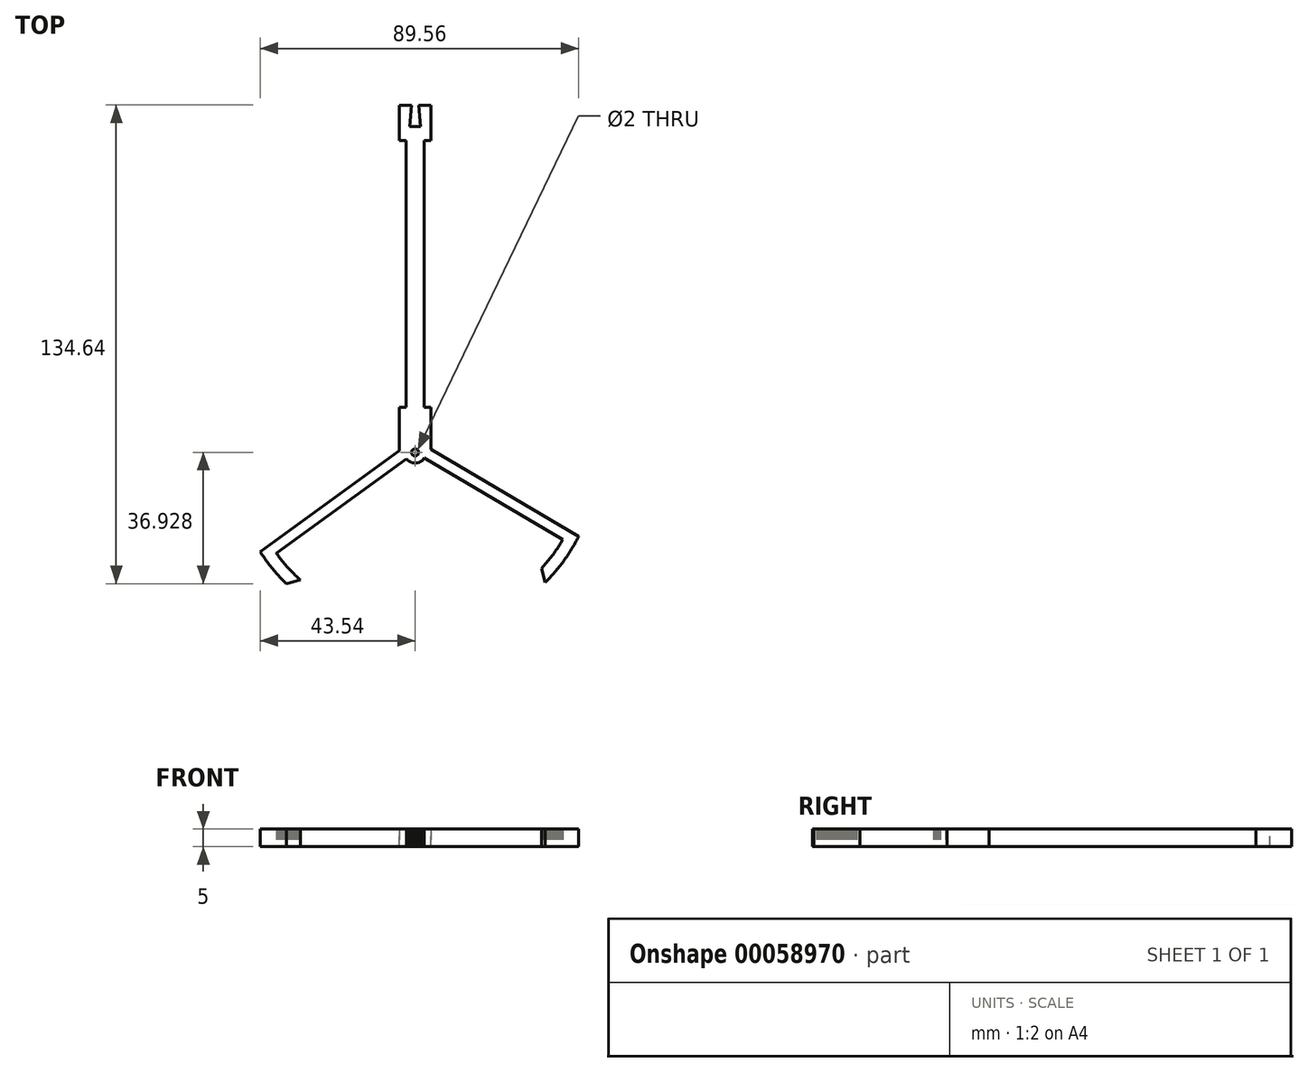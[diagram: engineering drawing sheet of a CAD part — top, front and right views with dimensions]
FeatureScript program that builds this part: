
annotation { "Feature Type Name" : "Feature", "Feature Type Description" : "" }
export const myFeature = defineFeature(function(context is Context, id is Id, definition is map)
    precondition{}
    {
        {
            var Q0;
            Q0=qCreatedBy(makeId("Top.planeOp"),FACE);
            var sketch = newSketch(context, id + "F0", { "sketchPlane" : qUnion([Q0])});
            skLineSegment(sketch, "E0.top", {"start": v(3.2, 29.68) * mm, "end": v(-5.68, 29.68) * mm});
            skLineSegment(sketch, "E0.left", {"start": v(3.2, 16.97) * mm, "end": v(3.2, 29.68) * mm});
            skLineSegment(sketch, "E0.right", {"start": v(-5.68, 16.97) * mm, "end": v(-5.68, 29.68) * mm});
            skLineSegment(sketch, "E1", {"start": v(-5.68, 16.97) * mm, "end": v(3.2, 16.97) * mm});
            skLineSegment(sketch, "E2", {"start": v(-33.5, -18.91) * mm, "end": v(-33.88, -18.58) * mm});
            skLineSegment(sketch, "E3", {"start": v(-33.88, -18.58) * mm, "end": v(-34.24, -18.24) * mm});
            skLineSegment(sketch, "E4", {"start": v(-34.24, -18.24) * mm, "end": v(-34.6, -17.9) * mm});
            skLineSegment(sketch, "E5", {"start": v(-34.6, -17.9) * mm, "end": v(-34.97, -17.55) * mm});
            skLineSegment(sketch, "E6", {"start": v(-34.97, -17.55) * mm, "end": v(-35.32, -17.2) * mm});
            skLineSegment(sketch, "E7", {"start": v(-35.32, -17.2) * mm, "end": v(-35.67, -16.84) * mm});
            skLineSegment(sketch, "E8", {"start": v(-35.67, -16.84) * mm, "end": v(-36.02, -16.48) * mm});
            skLineSegment(sketch, "E9", {"start": v(-36.02, -16.48) * mm, "end": v(-36.37, -16.12) * mm});
            skLineSegment(sketch, "E10", {"start": v(-36.37, -16.12) * mm, "end": v(-36.7, -15.75) * mm});
            skLineSegment(sketch, "E11", {"start": v(-36.7, -15.75) * mm, "end": v(-37.05, -15.38) * mm});
            skLineSegment(sketch, "E12", {"start": v(-37.05, -15.38) * mm, "end": v(-37.38, -15.01) * mm});
            skLineSegment(sketch, "E13", {"start": v(-37.38, -15.01) * mm, "end": v(-37.7, -14.64) * mm});
            skLineSegment(sketch, "E14", {"start": v(-37.7, -14.64) * mm, "end": v(-38.03, -14.26) * mm});
            skLineSegment(sketch, "E15", {"start": v(-38.03, -14.26) * mm, "end": v(-38.36, -13.87) * mm});
            skLineSegment(sketch, "E16", {"start": v(-38.36, -13.87) * mm, "end": v(-38.67, -13.49) * mm});
            skLineSegment(sketch, "E17", {"start": v(-38.67, -13.49) * mm, "end": v(-38.99, -13.1) * mm});
            skLineSegment(sketch, "E18", {"start": v(-38.99, -13.1) * mm, "end": v(-39.3, -12.7) * mm});
            skLineSegment(sketch, "E19", {"start": v(-39.3, -12.7) * mm, "end": v(-39.6, -12.3) * mm});
            skLineSegment(sketch, "E20", {"start": v(-39.6, -12.3) * mm, "end": v(-39.9, -11.9) * mm});
            skLineSegment(sketch, "E21", {"start": v(-39.9, -11.9) * mm, "end": v(-40.2, -11.5) * mm});
            skLineSegment(sketch, "E22", {"start": v(-40.2, -11.5) * mm, "end": v(-40.26, -11.42) * mm});
            skLineSegment(sketch, "E23", {"start": v(-40.26, -11.42) * mm, "end": v(-3.67, 15.2) * mm});
            skLineSegment(sketch, "E24", {"start": v(-3.67, 15.2) * mm, "end": v(-3.34, 14.82) * mm});
            skLineSegment(sketch, "E25", {"start": v(-3.34, 14.82) * mm, "end": v(-2.95, 14.5) * mm});
            skLineSegment(sketch, "E26", {"start": v(-2.95, 14.5) * mm, "end": v(-2.52, 14.25) * mm});
            skLineSegment(sketch, "E27", {"start": v(-2.52, 14.25) * mm, "end": v(-2.06, 14.08) * mm});
            skLineSegment(sketch, "E28", {"start": v(-2.06, 14.08) * mm, "end": v(-1.56, 13.98) * mm});
            skLineSegment(sketch, "E29", {"start": v(-1.56, 13.98) * mm, "end": v(-1.07, 13.97) * mm});
            skLineSegment(sketch, "E30", {"start": v(-1.07, 13.97) * mm, "end": v(-0.57, 14.04) * mm});
            skLineSegment(sketch, "E31", {"start": v(-0.57, 14.04) * mm, "end": v(-0.1, 14.2) * mm});
            skLineSegment(sketch, "E32", {"start": v(-0.1, 14.2) * mm, "end": v(0.35, 14.42) * mm});
            skLineSegment(sketch, "E33", {"start": v(0.35, 14.42) * mm, "end": v(0.75, 14.72) * mm});
            skLineSegment(sketch, "E34", {"start": v(0.75, 14.72) * mm, "end": v(1.1, 15.08) * mm});
            skLineSegment(sketch, "E35", {"start": v(1.1, 15.08) * mm, "end": v(1.34, 15.44) * mm});
            skLineSegment(sketch, "E36", {"start": v(1.34, 15.44) * mm, "end": v(40.32, -7.55) * mm});
            skLineSegment(sketch, "E37", {"start": v(40.32, -7.55) * mm, "end": v(40.07, -7.98) * mm});
            skLineSegment(sketch, "E38", {"start": v(40.07, -7.98) * mm, "end": v(39.8, -8.4) * mm});
            skLineSegment(sketch, "E39", {"start": v(39.8, -8.4) * mm, "end": v(39.54, -8.83) * mm});
            skLineSegment(sketch, "E40", {"start": v(39.54, -8.83) * mm, "end": v(39.27, -9.25) * mm});
            skLineSegment(sketch, "E41", {"start": v(39.27, -9.25) * mm, "end": v(39, -9.67) * mm});
            skLineSegment(sketch, "E42", {"start": v(39, -9.67) * mm, "end": v(38.72, -10.09) * mm});
            skLineSegment(sketch, "E43", {"start": v(38.72, -10.09) * mm, "end": v(38.44, -10.5) * mm});
            skLineSegment(sketch, "E44", {"start": v(38.44, -10.5) * mm, "end": v(38.15, -10.9) * mm});
            skLineSegment(sketch, "E45", {"start": v(38.15, -10.9) * mm, "end": v(37.86, -11.31) * mm});
            skLineSegment(sketch, "E46", {"start": v(37.86, -11.31) * mm, "end": v(37.57, -11.72) * mm});
            skLineSegment(sketch, "E47", {"start": v(37.57, -11.72) * mm, "end": v(37.27, -12.12) * mm});
            skLineSegment(sketch, "E48", {"start": v(37.27, -12.12) * mm, "end": v(36.96, -12.52) * mm});
            skLineSegment(sketch, "E49", {"start": v(36.96, -12.52) * mm, "end": v(36.65, -12.91) * mm});
            skLineSegment(sketch, "E50", {"start": v(36.65, -12.91) * mm, "end": v(36.34, -13.3) * mm});
            skLineSegment(sketch, "E51", {"start": v(36.34, -13.3) * mm, "end": v(36.03, -13.69) * mm});
            skLineSegment(sketch, "E52", {"start": v(36.03, -13.69) * mm, "end": v(35.7, -14.07) * mm});
            skLineSegment(sketch, "E53", {"start": v(35.7, -14.07) * mm, "end": v(35.38, -14.45) * mm});
            skLineSegment(sketch, "E54", {"start": v(35.38, -14.45) * mm, "end": v(35.06, -14.83) * mm});
            skLineSegment(sketch, "E55", {"start": v(35.06, -14.83) * mm, "end": v(34.73, -15.2) * mm});
            skLineSegment(sketch, "E56", {"start": v(34.73, -15.2) * mm, "end": v(34.4, -15.58) * mm});
            skLineSegment(sketch, "E57", {"start": v(34.4, -15.58) * mm, "end": v(34.32, -15.66) * mm});
            skLineSegment(sketch, "E58", {"start": v(34.32, -15.66) * mm, "end": v(35.33, -19.65) * mm});
            skLineSegment(sketch, "E59", {"start": v(35.33, -19.65) * mm, "end": v(35.68, -19.3) * mm});
            skLineSegment(sketch, "E60", {"start": v(35.68, -19.3) * mm, "end": v(36.03, -18.93) * mm});
            skLineSegment(sketch, "E61", {"start": v(36.03, -18.93) * mm, "end": v(36.37, -18.57) * mm});
            skLineSegment(sketch, "E62", {"start": v(36.37, -18.57) * mm, "end": v(36.72, -18.2) * mm});
            skLineSegment(sketch, "E63", {"start": v(36.72, -18.2) * mm, "end": v(37.05, -17.84) * mm});
            skLineSegment(sketch, "E64", {"start": v(37.05, -17.84) * mm, "end": v(37.39, -17.47) * mm});
            skLineSegment(sketch, "E65", {"start": v(37.39, -17.47) * mm, "end": v(37.72, -17.1) * mm});
            skLineSegment(sketch, "E66", {"start": v(37.72, -17.1) * mm, "end": v(38.05, -16.71) * mm});
            skLineSegment(sketch, "E67", {"start": v(38.05, -16.71) * mm, "end": v(38.37, -16.33) * mm});
            skLineSegment(sketch, "E68", {"start": v(38.37, -16.33) * mm, "end": v(38.69, -15.95) * mm});
            skLineSegment(sketch, "E69", {"start": v(38.69, -15.95) * mm, "end": v(39, -15.56) * mm});
            skLineSegment(sketch, "E70", {"start": v(39, -15.56) * mm, "end": v(39.32, -15.17) * mm});
            skLineSegment(sketch, "E71", {"start": v(39.32, -15.17) * mm, "end": v(39.63, -14.78) * mm});
            skLineSegment(sketch, "E72", {"start": v(39.63, -14.78) * mm, "end": v(39.93, -14.38) * mm});
            skLineSegment(sketch, "E73", {"start": v(39.93, -14.38) * mm, "end": v(40.23, -13.98) * mm});
            skLineSegment(sketch, "E74", {"start": v(40.23, -13.98) * mm, "end": v(40.53, -13.58) * mm});
            skLineSegment(sketch, "E75", {"start": v(40.53, -13.58) * mm, "end": v(40.82, -13.17) * mm});
            skLineSegment(sketch, "E76", {"start": v(40.82, -13.17) * mm, "end": v(41.11, -12.77) * mm});
            skLineSegment(sketch, "E77", {"start": v(41.11, -12.77) * mm, "end": v(41.4, -12.35) * mm});
            skLineSegment(sketch, "E78", {"start": v(41.4, -12.35) * mm, "end": v(41.68, -11.94) * mm});
            skLineSegment(sketch, "E79", {"start": v(41.68, -11.94) * mm, "end": v(41.96, -11.53) * mm});
            skLineSegment(sketch, "E80", {"start": v(41.96, -11.53) * mm, "end": v(42.23, -11.1) * mm});
            skLineSegment(sketch, "E81", {"start": v(42.23, -11.1) * mm, "end": v(42.5, -10.69) * mm});
            skLineSegment(sketch, "E82", {"start": v(42.5, -10.69) * mm, "end": v(42.76, -10.26) * mm});
            skLineSegment(sketch, "E83", {"start": v(42.76, -10.26) * mm, "end": v(43.02, -9.83) * mm});
            skLineSegment(sketch, "E84", {"start": v(43.02, -9.83) * mm, "end": v(43.28, -9.4) * mm});
            skLineSegment(sketch, "E85", {"start": v(43.28, -9.4) * mm, "end": v(43.53, -8.97) * mm});
            skLineSegment(sketch, "E86", {"start": v(43.53, -8.97) * mm, "end": v(43.78, -8.54) * mm});
            skLineSegment(sketch, "E87", {"start": v(43.78, -8.54) * mm, "end": v(44.03, -8.1) * mm});
            skLineSegment(sketch, "E88", {"start": v(44.03, -8.1) * mm, "end": v(44.27, -7.67) * mm});
            skLineSegment(sketch, "E89", {"start": v(44.27, -7.67) * mm, "end": v(44.5, -7.22) * mm});
            skLineSegment(sketch, "E90", {"start": v(44.5, -7.22) * mm, "end": v(44.73, -6.78) * mm});
            skLineSegment(sketch, "E91", {"start": v(44.73, -6.78) * mm, "end": v(44.78, -6.7) * mm});
            skLineSegment(sketch, "E92", {"start": v(44.78, -6.7) * mm, "end": v(0.28, 19.55) * mm});
            skLineSegment(sketch, "E93", {"start": v(0.28, 19.55) * mm, "end": v(-0.17, 19.77) * mm});
            skLineSegment(sketch, "E94", {"start": v(-0.17, 19.77) * mm, "end": v(-0.65, 19.9) * mm});
            skLineSegment(sketch, "E95", {"start": v(-0.65, 19.9) * mm, "end": v(-1.14, 19.96) * mm});
            skLineSegment(sketch, "E96", {"start": v(-1.14, 19.96) * mm, "end": v(-1.64, 19.94) * mm});
            skLineSegment(sketch, "E97", {"start": v(-1.64, 19.94) * mm, "end": v(-2.13, 19.83) * mm});
            skLineSegment(sketch, "E98", {"start": v(-2.13, 19.83) * mm, "end": v(-2.6, 19.64) * mm});
            skLineSegment(sketch, "E99", {"start": v(-2.6, 19.64) * mm, "end": v(-3, 19.4) * mm});
            skLineSegment(sketch, "E100", {"start": v(-3, 19.4) * mm, "end": v(-44.78, -11) * mm});
            skLineSegment(sketch, "E101", {"start": v(-44.78, -11) * mm, "end": v(-44.5, -11.42) * mm});
            skLineSegment(sketch, "E102", {"start": v(-44.5, -11.42) * mm, "end": v(-44.23, -11.83) * mm});
            skLineSegment(sketch, "E103", {"start": v(-44.23, -11.83) * mm, "end": v(-43.95, -12.25) * mm});
            skLineSegment(sketch, "E104", {"start": v(-43.95, -12.25) * mm, "end": v(-43.67, -12.66) * mm});
            skLineSegment(sketch, "E105", {"start": v(-43.67, -12.66) * mm, "end": v(-43.38, -13.07) * mm});
            skLineSegment(sketch, "E106", {"start": v(-43.38, -13.07) * mm, "end": v(-43.09, -13.47) * mm});
            skLineSegment(sketch, "E107", {"start": v(-43.09, -13.47) * mm, "end": v(-42.79, -13.88) * mm});
            skLineSegment(sketch, "E108", {"start": v(-42.79, -13.88) * mm, "end": v(-42.49, -14.28) * mm});
            skLineSegment(sketch, "E109", {"start": v(-42.49, -14.28) * mm, "end": v(-42.19, -14.67) * mm});
            skLineSegment(sketch, "E110", {"start": v(-42.19, -14.67) * mm, "end": v(-41.88, -15.07) * mm});
            skLineSegment(sketch, "E111", {"start": v(-41.88, -15.07) * mm, "end": v(-41.57, -15.46) * mm});
            skLineSegment(sketch, "E112", {"start": v(-41.57, -15.46) * mm, "end": v(-41.25, -15.85) * mm});
            skLineSegment(sketch, "E113", {"start": v(-41.25, -15.85) * mm, "end": v(-40.93, -16.23) * mm});
            skLineSegment(sketch, "E114", {"start": v(-40.93, -16.23) * mm, "end": v(-40.6, -16.61) * mm});
            skLineSegment(sketch, "E115", {"start": v(-40.6, -16.61) * mm, "end": v(-40.28, -17) * mm});
            skLineSegment(sketch, "E116", {"start": v(-40.28, -17) * mm, "end": v(-39.95, -17.37) * mm});
            skLineSegment(sketch, "E117", {"start": v(-39.95, -17.37) * mm, "end": v(-39.62, -17.74) * mm});
            skLineSegment(sketch, "E118", {"start": v(-39.62, -17.74) * mm, "end": v(-39.28, -18.11) * mm});
            skLineSegment(sketch, "E119", {"start": v(-39.28, -18.11) * mm, "end": v(-38.94, -18.48) * mm});
            skLineSegment(sketch, "E120", {"start": v(-38.94, -18.48) * mm, "end": v(-38.6, -18.84) * mm});
            skLineSegment(sketch, "E121", {"start": v(-38.6, -18.84) * mm, "end": v(-38.25, -19.2) * mm});
            skLineSegment(sketch, "E122", {"start": v(-38.25, -19.2) * mm, "end": v(-37.9, -19.55) * mm});
            skLineSegment(sketch, "E123", {"start": v(-37.9, -19.55) * mm, "end": v(-37.54, -19.9) * mm});
            skLineSegment(sketch, "E124", {"start": v(-37.54, -19.9) * mm, "end": v(-37.49, -19.96) * mm});
            skLineSegment(sketch, "E125", {"start": v(-37.49, -19.96) * mm, "end": v(-33.5, -18.91) * mm});
            skLineSegment(sketch, "E126", {"start": v(-2.24, 16.97) * mm, "end": v(-0.24, 16.97) * mm, "construction": true});
            skPoint(sketch, "E127", {"position": v(-1.24, 16.97) * mm});
            skCircle(sketch, "E128", {"center": v(-1.24, 16.97) * mm, "radius": 1 * mm});
            skSolve(sketch);
        }
        {
            var Q0;
            Q0=qSketchRegion(id+"F0",true);
            extrude(context, id + "F1", {"entities" : qUnion([Q0]), "depth" : 5 * mm});
        }
        {
            var Q0;
            Q0=makeQuery(id+"F1.opExtrude","SWEPT_FACE",FACE,{"disambiguationData":[OSD([sQuery(id+"F0.wireOp",EDGE,"E0.top")])]});
            var sketch = newSketch(context, id + "F2", { "sketchPlane" : qUnion([Q0])});
            skLineSegment(sketch, "E129.bottom", {"start": v(-3.2, 5) * mm, "end": v(5.68, 5) * mm, "construction": true});
            skLineSegment(sketch, "E129.top", {"start": v(-3.2, 0) * mm, "end": v(5.68, 0) * mm, "construction": true});
            skLineSegment(sketch, "E129.left", {"start": v(-3.2, 5) * mm, "end": v(-3.2, 0) * mm, "construction": true});
            skLineSegment(sketch, "E129.right", {"start": v(5.68, 5) * mm, "end": v(5.68, 0) * mm, "construction": true});
            skLineSegment(sketch, "E130", {"start": v(1.24, 5) * mm, "end": v(1.24, 0) * mm, "construction": true});
            skPoint(sketch, "E131", {"position": v(1.24, 2.5) * mm});
            skLineSegment(sketch, "E132.bottom", {"start": v(-1.26, 5) * mm, "end": v(3.74, 5) * mm});
            skLineSegment(sketch, "E132.top", {"start": v(-1.26, 0) * mm, "end": v(3.74, 0) * mm});
            skLineSegment(sketch, "E132.left", {"start": v(-1.26, 5) * mm, "end": v(-1.26, 0) * mm});
            skLineSegment(sketch, "E132.right", {"start": v(3.74, 5) * mm, "end": v(3.74, 0) * mm});
            skPoint(sketch, "E133", {"position": v(1.24, 5) * mm});
            skSolve(sketch);
        }
        {
            var Q0;
            Q0=makeQuery(id+"F2.imprint","IMPRINT",FACE,{"disambiguationData":[TD([[makeQuery(id+"F2.imprint","IMPRINT",EDGE,{"derivedFrom":sQuery(id+"F2.wireOp",EDGE,"E132.bottom")}),-1.0]])]});
            extrude(context, id + "F3", {"entities" : qUnion([Q0]), "operationType" : NewBodyOperationType.ADD, "depth" : 85 * mm});
        }
        {
            var Q0;
            Q0=makeQuery(id+"F3.boolean.opBoolean","MERGE",FACE,{"derivedFrom":[makeQuery(id+"F1.opExtrude","CAP_FACE",FACE,{"disambiguationData":[OSD([sQuery(id+"F0.wireOp",EDGE,"d9f391bc-674f-497b-be90-560cbfe84b75"),sQuery(id+"F0.wireOp",EDGE,"66b45562-6a73-478d-960d-9298d4f6f7f0"),sQuery(id+"F0.wireOp",EDGE,"14187485-9066-4405-92d3-fc27601e42af"),sQuery(id+"F0.wireOp",EDGE,"531d857a-c366-4fd6-946f-2a201ec59503"),sQuery(id+"F0.wireOp",EDGE,"82b77f9d-e961-41ac-b487-f27284012814"),sQuery(id+"F0.wireOp",EDGE,"7834417a-5e7c-45c5-8e6f-19fbc39ef538"),sQuery(id+"F0.wireOp",EDGE,"300af05a-1d2d-4a39-b159-b80513d7f740"),sQuery(id+"F0.wireOp",EDGE,"1d5f7e8b-d76f-446f-8b3e-2a2f550bd8e3"),sQuery(id+"F0.wireOp",EDGE,"35e8518a-73fa-4b07-8810-64eb534e7b1e"),sQuery(id+"F0.wireOp",EDGE,"18614789-dbbf-47a7-80e0-906205be91d2"),sQuery(id+"F0.wireOp",EDGE,"b77e8b2d-b58d-4b65-9e12-d4334338aa4c"),sQuery(id+"F0.wireOp",EDGE,"9d96ad04-3b06-4638-bbb7-3f0403701198"),sQuery(id+"F0.wireOp",EDGE,"e2f941ec-7ca7-4e10-9b82-3674a8dee568"),sQuery(id+"F0.wireOp",EDGE,"623cfd6c-6096-4034-a234-787e3acb7919"),sQuery(id+"F0.wireOp",EDGE,"effc0b7c-bb45-4b4c-82cf-5a194e7747a9"),sQuery(id+"F0.wireOp",EDGE,"20afc2aa-4987-4b9c-837f-1a90a823d70c"),sQuery(id+"F0.wireOp",EDGE,"93c108a5-420a-46d6-a4f1-9fc166012f6e"),sQuery(id+"F0.wireOp",EDGE,"24f54e41-abe2-49ed-aca4-37dbfc811c90"),sQuery(id+"F0.wireOp",EDGE,"9775e243-409f-4585-bc05-4883512e3564"),sQuery(id+"F0.wireOp",EDGE,"a5e87a16-9f3d-4e96-afb7-1f3010025381"),sQuery(id+"F0.wireOp",EDGE,"57da4376-ad28-41da-a036-1c08f5a0e9fe"),sQuery(id+"F0.wireOp",EDGE,"42ac5c60-1a59-4eb0-a50e-105db2941719"),sQuery(id+"F0.wireOp",EDGE,"7f869c91-c514-4a78-955d-8fa2f71ec013"),sQuery(id+"F0.wireOp",EDGE,"92df5dc1-1633-40e4-82dc-26b14e9fc4fe"),sQuery(id+"F0.wireOp",EDGE,"9fb6344f-8160-4d43-a8ca-7dc5bcb63cf4"),sQuery(id+"F0.wireOp",EDGE,"403433ed-74ab-49ef-b5f3-8321a2a46bc0"),sQuery(id+"F0.wireOp",EDGE,"38791a52-10f3-4032-89cb-9997d4a285ff"),sQuery(id+"F0.wireOp",EDGE,"17827bc5-de02-4b8f-ae35-e25ffe9a3a56"),sQuery(id+"F0.wireOp",EDGE,"ebb8a741-28c9-44e3-8d01-7b9906950363"),sQuery(id+"F0.wireOp",EDGE,"24247562-824f-4080-b562-a07a46203f45"),sQuery(id+"F0.wireOp",EDGE,"61158206-3902-44f4-b84a-59a3b62cea53"),sQuery(id+"F0.wireOp",EDGE,"222b9068-06c2-468c-a816-7dcc0e9861e7"),sQuery(id+"F0.wireOp",EDGE,"1443c47e-cb78-4972-aa1d-b2a5593cacaa"),sQuery(id+"F0.wireOp",EDGE,"4ee5fa2a-e4b7-4507-9879-d4257c452374"),sQuery(id+"F0.wireOp",EDGE,"ac129c3d-c943-4e23-b628-d4f0035e9390"),sQuery(id+"F0.wireOp",EDGE,"a4b60933-6dc5-485c-afad-bad217473213"),sQuery(id+"F0.wireOp",EDGE,"c784899e-bd4b-4296-9021-59274ccaadd9"),sQuery(id+"F0.wireOp",EDGE,"748fc19f-7cd7-4142-921c-8b19d610d3d1"),sQuery(id+"F0.wireOp",EDGE,"ebea3f07-4c38-41c4-ac2c-bac9cb8d1528"),sQuery(id+"F0.wireOp",EDGE,"c6bc3915-ea64-408b-b0c0-442b260292ac"),sQuery(id+"F0.wireOp",EDGE,"15593884-b140-4daf-bfd8-0ecfa5efcbbd"),sQuery(id+"F0.wireOp",EDGE,"a7df4056-7cd6-44bf-9033-605bc9c32d03"),sQuery(id+"F0.wireOp",EDGE,"39d318a8-1c2b-49b4-b444-523ba4d5fcf2"),sQuery(id+"F0.wireOp",EDGE,"11df0492-6635-41a9-8511-0c760388fa34"),sQuery(id+"F0.wireOp",EDGE,"a12d8f92-446a-4b34-a2f5-26c26993d257"),sQuery(id+"F0.wireOp",EDGE,"78a7d225-68f4-4e83-b71e-32c50f125e93"),sQuery(id+"F0.wireOp",EDGE,"1862a963-57d5-471d-8109-9f73d1aa8848"),sQuery(id+"F0.wireOp",EDGE,"54f45445-f8d1-4aff-bece-9da66ad386cd"),sQuery(id+"F0.wireOp",EDGE,"5ba05bdf-983b-4f68-941c-4bf50adfb3c5"),sQuery(id+"F0.wireOp",EDGE,"973eaeb2-d25f-40eb-b74f-e363d637089d"),sQuery(id+"F0.wireOp",EDGE,"9fe65cb9-7a78-4622-86d1-7f23de040810"),sQuery(id+"F0.wireOp",EDGE,"3fe47919-788c-4396-b5fd-8990ec275c22"),sQuery(id+"F0.wireOp",EDGE,"55bf8aa7-cfd1-4645-9e83-de087904feb2"),sQuery(id+"F0.wireOp",EDGE,"c2af9e0f-cc3a-474c-a54e-54ce149af3bb"),sQuery(id+"F0.wireOp",EDGE,"ff518af7-eed7-424f-ad46-c5242196626b"),sQuery(id+"F0.wireOp",EDGE,"cc0332f5-aef5-4de5-a14e-8dcbe21eca6c"),sQuery(id+"F0.wireOp",EDGE,"c5d08f8f-8ed2-45eb-9a75-cb5f251a4d6d"),sQuery(id+"F0.wireOp",EDGE,"5995e242-d37b-4450-9f63-962c7eb38085"),sQuery(id+"F0.wireOp",EDGE,"25f3b115-5ae4-4790-92e5-62a7bc3f5c29"),sQuery(id+"F0.wireOp",EDGE,"2d611a70-a2f5-475a-a6a8-adddd76473ce"),sQuery(id+"F0.wireOp",EDGE,"273bf26d-3f66-4ef4-bf64-d22a533f903a"),sQuery(id+"F0.wireOp",EDGE,"de5f23e0-e1a0-4e15-900e-688ab9168dcd"),sQuery(id+"F0.wireOp",EDGE,"4de6b542-ff3a-44f7-b58e-1e4f3b2cccf4"),sQuery(id+"F0.wireOp",EDGE,"be1b36f0-e020-4af0-baec-c4481b6b9122"),sQuery(id+"F0.wireOp",EDGE,"d7c1d08a-2f0c-4649-94c4-8f89162c768a"),sQuery(id+"F0.wireOp",EDGE,"bd09b6b8-9bc9-4c5b-ab2b-4ede4d9b9cae"),sQuery(id+"F0.wireOp",EDGE,"05b5a1f0-0223-4439-ac6f-cac7d6a05357"),sQuery(id+"F0.wireOp",EDGE,"318e3676-c449-41e0-b4da-e74d07fc2b12"),sQuery(id+"F0.wireOp",EDGE,"31725f89-0695-4483-9200-5756053d80e4"),sQuery(id+"F0.wireOp",EDGE,"e3cb0712-5583-40de-9f57-2bae5fcde790"),sQuery(id+"F0.wireOp",EDGE,"c6456fea-21fc-4931-a427-a856d1f6ee5c"),sQuery(id+"F0.wireOp",EDGE,"e7d8b0b0-a421-4050-b770-ef5136dc3e4d"),sQuery(id+"F0.wireOp",EDGE,"0788d0b0-f754-45d8-aefc-a91755a03ac1"),sQuery(id+"F0.wireOp",EDGE,"fc27efed-591c-43cc-b4b2-6872e1742544"),sQuery(id+"F0.wireOp",EDGE,"82c2f9b8-58bc-4a33-9bd5-fec435af3e72"),sQuery(id+"F0.wireOp",EDGE,"2e300663-fb6b-4f29-9ebf-a9fab34af9c4"),sQuery(id+"F0.wireOp",EDGE,"3d2dfd07-a0b9-43b8-893f-685d0a355372"),sQuery(id+"F0.wireOp",EDGE,"e776ef69-6530-4f3d-8924-f9840dcd9e4d"),sQuery(id+"F0.wireOp",EDGE,"6dcbcc22-e493-4400-9b8a-7eed73031bc4"),sQuery(id+"F0.wireOp",EDGE,"7cdd9895-84d3-47ea-86bd-688608d79eca"),sQuery(id+"F0.wireOp",EDGE,"3a7bfdfd-3144-4dae-8888-a8bcf2221552"),sQuery(id+"F0.wireOp",EDGE,"2953d7e0-23a1-472e-bf8c-49982d9a56d6"),sQuery(id+"F0.wireOp",EDGE,"846718aa-0a8a-476e-8a52-f2d355658347"),sQuery(id+"F0.wireOp",EDGE,"13e02fad-2dbd-4394-a12b-883b621fb0cf"),sQuery(id+"F0.wireOp",EDGE,"9bfc4f6e-5194-4c80-9375-02c13d7037c7"),sQuery(id+"F0.wireOp",EDGE,"4cc90906-b22a-4bfe-9933-4a2b42c67043"),sQuery(id+"F0.wireOp",EDGE,"c3968d64-93bc-4dc6-b8a7-840e206f0e92"),sQuery(id+"F0.wireOp",EDGE,"cff9c3c0-4237-426c-aea8-7115d6da3525"),sQuery(id+"F0.wireOp",EDGE,"76e5b534-b14d-4a45-9111-d87c94f3d3da"),sQuery(id+"F0.wireOp",EDGE,"96eb4b59-6d18-41e9-8181-93777d457c04"),sQuery(id+"F0.wireOp",EDGE,"4b80822d-625d-4929-946d-bb2fee906de1"),sQuery(id+"F0.wireOp",EDGE,"a1b1815c-0f60-4723-aacc-aafe0ccbf065"),sQuery(id+"F0.wireOp",EDGE,"63631a9c-c3d0-4e34-b42e-cf718a2aa654"),sQuery(id+"F0.wireOp",EDGE,"291662e0-8a9a-4794-9b05-15f69232fded"),sQuery(id+"F0.wireOp",EDGE,"c31bbd6a-e51d-4bda-bb55-a930242c1aae"),sQuery(id+"F0.wireOp",EDGE,"6cc65a5c-01cd-414d-b4bf-16365d086d8b"),sQuery(id+"F0.wireOp",EDGE,"0f6044bc-5aed-4332-8dd0-ed4f837cf9c8"),sQuery(id+"F0.wireOp",EDGE,"68f51909-fb33-4c21-8354-d3ee43222832"),sQuery(id+"F0.wireOp",EDGE,"0ba4c335-165f-4c3e-a523-b257962ab2b9"),sQuery(id+"F0.wireOp",EDGE,"a8ab603d-6f8c-4c2b-bc3e-a90f3d25e983"),sQuery(id+"F0.wireOp",EDGE,"3346a9eb-c449-4294-82ff-d0765618b8c3"),sQuery(id+"F0.wireOp",EDGE,"efd91459-38fa-452e-891e-edab332f6489"),sQuery(id+"F0.wireOp",EDGE,"85b94afd-6a00-47ab-a374-eb0a6b957af6"),sQuery(id+"F0.wireOp",EDGE,"71bbe033-8d0c-4649-8752-095e423e4446"),sQuery(id+"F0.wireOp",EDGE,"313f4505-8deb-44f7-a07b-deab9fdd4fca"),sQuery(id+"F0.wireOp",EDGE,"58514e34-5bb3-46cf-af5d-05d66b0c10f9"),sQuery(id+"F0.wireOp",EDGE,"9c61e8f2-2ab1-4688-a9d6-5c20a88d6f6a"),sQuery(id+"F0.wireOp",EDGE,"f84fcc24-327f-4d24-8afc-1352f07d6813"),sQuery(id+"F0.wireOp",EDGE,"2217ef4b-fa2d-4c42-8d86-ed7db710f5bd"),sQuery(id+"F0.wireOp",EDGE,"d87f30a8-b645-4562-81e4-3c3cf9cd6438"),sQuery(id+"F0.wireOp",EDGE,"6b1cc9ff-038e-4fc2-952b-8fefe25711b2"),sQuery(id+"F0.wireOp",EDGE,"9b0d0940-50e4-4c60-959e-8cb1c47cda3d"),sQuery(id+"F0.wireOp",EDGE,"fd67a80c-15d7-4a10-bc2d-74f667f92aae"),sQuery(id+"F0.wireOp",EDGE,"ce9cbc48-37c6-4742-bee7-228e45a917e3"),sQuery(id+"F0.wireOp",EDGE,"668236f6-3d49-4ccf-890f-7b693b95a113"),sQuery(id+"F0.wireOp",EDGE,"f978c870-af19-49dc-a3f6-58e714ba6b8d"),sQuery(id+"F0.wireOp",EDGE,"3c9fd5d7-5c91-4e2a-8e90-77909dfb583b"),sQuery(id+"F0.wireOp",EDGE,"3f653433-d41a-442d-9af1-f4ba11755801"),sQuery(id+"F0.wireOp",EDGE,"3e1bc7f2-4028-408e-8046-60d3c4eab3db"),sQuery(id+"F0.wireOp",EDGE,"6e5cb531-4b2f-424d-b6a2-fd274bbfcedc"),sQuery(id+"F0.wireOp",EDGE,"47450d10-22bf-4260-9408-7e53fd283f2d"),sQuery(id+"F0.wireOp",EDGE,"6d45c327-3d4d-4948-b28d-f57c85b01b79"),sQuery(id+"F0.wireOp",EDGE,"09a427cb-33ca-4fdc-b261-2336e21235b2"),sQuery(id+"F0.wireOp",EDGE,"518944ec-1655-4f40-b183-544c6dabeccc"),sQuery(id+"F0.wireOp",EDGE,"9a21c479-1b04-474c-b49a-7bb92b3e97ee"),sQuery(id+"F0.wireOp",EDGE,"96faa4f8-2343-44d0-b0c9-daf9f0cf2026"),sQuery(id+"F0.wireOp",EDGE,"6fc17f55-5333-4b57-a339-275bf10e1425"),sQuery(id+"F0.wireOp",EDGE,"42fdd7f3-cbb8-400e-a0d9-d82489298c17"),sQuery(id+"F0.wireOp",EDGE,"ff3833a1-8283-4137-914b-97420855596c"),sQuery(id+"F0.wireOp",EDGE,"6d86c47c-1e01-4b32-ae2a-396aeb5aa8c3"),sQuery(id+"F0.wireOp",EDGE,"3656029b-9af7-4a6b-91c7-0cb8f82c84b0"),sQuery(id+"F0.wireOp",EDGE,"c5a5c181-3903-47b5-9841-0451d0b8c190"),sQuery(id+"F0.wireOp",EDGE,"6b476b77-b2de-421b-b26d-88dcbb17dccc"),sQuery(id+"F0.wireOp",EDGE,"3d318069-a1b2-4ca5-910a-b32c13e6ff0f"),sQuery(id+"F0.wireOp",EDGE,"9330180f-a560-47bb-918b-d92eebda0b31"),sQuery(id+"F0.wireOp",EDGE,"b318f770-8e99-4d49-b667-ae16576ab8c5"),sQuery(id+"F0.wireOp",EDGE,"e8c7022b-339d-4a50-8e2c-c0ad6522d806"),sQuery(id+"F0.wireOp",EDGE,"e86b4955-e698-4ab7-84b9-7f9632085e45"),sQuery(id+"F0.wireOp",EDGE,"0c38cf30-4431-4dda-a171-e1c8e016ea24"),sQuery(id+"F0.wireOp",EDGE,"f094b2ba-6a66-4d13-8490-6bb0ce785aa8"),sQuery(id+"F0.wireOp",EDGE,"41e1ebd6-8c90-401f-a72a-f212800231e3"),sQuery(id+"F0.wireOp",EDGE,"40e70cb6-71ec-4d67-b914-e8ee82708b93"),sQuery(id+"F0.wireOp",EDGE,"13f06e0a-f10b-47e7-959c-6b309f65aed5"),sQuery(id+"F0.wireOp",EDGE,"3fa473f8-a0ea-440b-8ccf-443d736f73d8"),sQuery(id+"F0.wireOp",EDGE,"3ff53a63-1f71-4b9e-b5b1-fe861864c7b9"),sQuery(id+"F0.wireOp",EDGE,"9fd11a8c-801f-433b-8a68-149d040764ea"),sQuery(id+"F0.wireOp",EDGE,"2b57bb01-2787-4d2a-a1f7-a8f2ac708940"),sQuery(id+"F0.wireOp",EDGE,"b3a649f2-00b2-4941-a5f4-54f2790e47c9"),sQuery(id+"F0.wireOp",EDGE,"689af078-1fc4-4801-82f7-c259a968d8e3"),sQuery(id+"F0.wireOp",EDGE,"4afb566c-1766-4da3-aeca-2e561b661cbf"),sQuery(id+"F0.wireOp",EDGE,"afbdcd0b-9ccb-41a6-b5df-fe1bcf30544d"),sQuery(id+"F0.wireOp",EDGE,"0a1a2607-09d2-45da-b494-66f0f4572d53"),sQuery(id+"F0.wireOp",EDGE,"df9dc95f-9734-4203-a4b0-b50527c86d60"),sQuery(id+"F0.wireOp",EDGE,"868db6a5-4ab0-468d-816c-25f0bc18b053"),sQuery(id+"F0.wireOp",EDGE,"aaa1c0b5-afc6-4e25-82a0-d6f0aaf8ec45"),sQuery(id+"F0.wireOp",EDGE,"450ffb83-aa88-433e-99e9-7fc4bc443133"),sQuery(id+"F0.wireOp",EDGE,"7c9dc92b-bdbd-4c2f-ba2f-b681be311a02"),sQuery(id+"F0.wireOp",EDGE,"d8d805bb-8432-4448-99fe-12ddf517f87f"),sQuery(id+"F0.wireOp",EDGE,"e1c897c1-2833-4eab-81cd-6ccc64de02e8"),sQuery(id+"F0.wireOp",EDGE,"12eef9dd-bb38-451e-8b46-68758d02cc0e"),sQuery(id+"F0.wireOp",EDGE,"f6b90299-a189-4960-beb2-75c4f087d852"),sQuery(id+"F0.wireOp",EDGE,"d44cce74-31fd-4baf-a4a6-ccbb4521b524"),sQuery(id+"F0.wireOp",EDGE,"26311da7-8aed-42c2-aa0d-06719439663e"),sQuery(id+"F0.wireOp",EDGE,"bfe2dd46-ca33-42a6-b3e5-4bcb679aff27"),sQuery(id+"F0.wireOp",EDGE,"f7121924-5964-4ee7-8e7a-9366b6055faf"),sQuery(id+"F0.wireOp",EDGE,"baddc95a-3768-4696-a9fc-c3c93e777550"),sQuery(id+"F0.wireOp",EDGE,"4cbcd0b8-8d3f-4500-b314-949e4192bba6"),sQuery(id+"F0.wireOp",EDGE,"573feae8-dbb2-4ee3-84b1-a2f0e784b4ce"),sQuery(id+"F0.wireOp",EDGE,"1491502b-4fac-4339-bddb-72d872b244a9"),sQuery(id+"F0.wireOp",EDGE,"ed8966f0-f9a2-415f-b3ef-00e8bec5a987"),sQuery(id+"F0.wireOp",EDGE,"42659012-de86-4715-a0b8-c198bc09b6c3"),sQuery(id+"F0.wireOp",EDGE,"eba869ca-ba70-4ef3-90af-459470689084"),sQuery(id+"F0.wireOp",EDGE,"9875f08d-c713-4704-93cd-788487ec0e6b"),sQuery(id+"F0.wireOp",EDGE,"88c7c1a6-46c1-45f7-a284-4e760e0ff227"),sQuery(id+"F0.wireOp",EDGE,"7296298e-4422-4531-89ec-245f94a1b7ce"),sQuery(id+"F0.wireOp",EDGE,"d982fd75-f615-4661-88e5-4d338e35f5d6"),sQuery(id+"F0.wireOp",EDGE,"855cb7c2-4006-4b69-ae1d-061ed893761e"),sQuery(id+"F0.wireOp",EDGE,"25f14cae-63dd-43dd-a2cf-069ce091aab3"),sQuery(id+"F0.wireOp",EDGE,"8dd2c990-ce8b-4ae6-88a5-6f7d81b76fb7"),sQuery(id+"F0.wireOp",EDGE,"50c487b6-7ae5-43ad-9b89-c44e1cfbe420"),sQuery(id+"F0.wireOp",EDGE,"28defd30-3f37-4457-b5ce-98c8ab6f0938"),sQuery(id+"F0.wireOp",EDGE,"25b26be1-608d-4fca-8147-ce63c78e7ef9"),sQuery(id+"F0.wireOp",EDGE,"55286520-3f9c-4cb0-8993-b41f90c1e7b2"),sQuery(id+"F0.wireOp",EDGE,"8b04d12e-496a-4f5a-9f87-f93561172584"),sQuery(id+"F0.wireOp",EDGE,"69f61a6b-229e-4c46-8902-5dacc0b3caa7"),sQuery(id+"F0.wireOp",EDGE,"b70ecf2a-3e9d-42b0-a09c-c895f72a43f5"),sQuery(id+"F0.wireOp",EDGE,"b4318e1e-f674-42cb-b4b4-c6a7f0d1058b"),sQuery(id+"F0.wireOp",EDGE,"0a5737aa-f65d-4c08-8fa3-74cd1c6bc787"),sQuery(id+"F0.wireOp",EDGE,"2b114e95-5b76-41c0-af98-aa6b4118be67"),sQuery(id+"F0.wireOp",EDGE,"909ff558-2fcb-4b4a-b58c-44165d3143ec"),sQuery(id+"F0.wireOp",EDGE,"03647ff9-6972-4830-a77b-507609320f8a"),sQuery(id+"F0.wireOp",EDGE,"784304f5-69fc-4c5d-a15a-a01099708ad1"),sQuery(id+"F0.wireOp",EDGE,"7e862998-cb3b-43fa-98f0-afa86e38354f"),sQuery(id+"F0.wireOp",EDGE,"b133dd31-da7f-4d34-b041-a02e12d47f77"),sQuery(id+"F0.wireOp",EDGE,"c20fe978-2982-45a4-865c-b8fa9effb66d"),sQuery(id+"F0.wireOp",EDGE,"ecc07ede-e418-4cc6-ac17-b0618c730539"),sQuery(id+"F0.wireOp",EDGE,"a72532f4-d06f-446a-a491-5e0e52dccc34"),sQuery(id+"F0.wireOp",EDGE,"e80db44c-f0a2-44c0-9d9a-ac9ec1fdb025"),sQuery(id+"F0.wireOp",EDGE,"a256cc86-e2ce-4537-87d8-996e6a32e2c3"),sQuery(id+"F0.wireOp",EDGE,"9d600fab-17dd-4d7f-9bf9-2e90aad73a65"),sQuery(id+"F0.wireOp",EDGE,"5042385b-9870-4c5e-be6a-0c3db3c46120"),sQuery(id+"F0.wireOp",EDGE,"31a5a34f-51f7-4c3e-8b64-8b1dabd0146e"),sQuery(id+"F0.wireOp",EDGE,"6b2aa247-f6cb-4ed4-b715-b1f137de6caf"),sQuery(id+"F0.wireOp",EDGE,"66b72c40-0d5e-4a0b-9279-31ab5fa1e7fe"),sQuery(id+"F0.wireOp",EDGE,"15e6370f-fd6b-4262-9e07-4cd19af6e575"),sQuery(id+"F0.wireOp",EDGE,"42ae2dfc-64aa-47e2-8300-2f233e3b2cdc"),sQuery(id+"F0.wireOp",EDGE,"f1330061-7111-4682-b376-6b8410619920"),sQuery(id+"F0.wireOp",EDGE,"4f299f36-5b62-45e5-935a-49dea53b4436"),sQuery(id+"F0.wireOp",EDGE,"f4a1d07d-759c-4b8c-a361-16f86e8a581b"),sQuery(id+"F0.wireOp",EDGE,"a197af79-e1d5-4cc2-bcad-7eec1b0bb374"),sQuery(id+"F0.wireOp",EDGE,"0b645705-9a78-41e4-bf43-11811c5310d6"),sQuery(id+"F0.wireOp",EDGE,"3b8b7332-f98f-4427-9e20-b42ec5fb5940"),sQuery(id+"F0.wireOp",EDGE,"dac7c135-5026-46cf-917a-981712ef2904"),sQuery(id+"F0.wireOp",EDGE,"e792f283-39e8-4103-9782-e05d206dbdd8"),sQuery(id+"F0.wireOp",EDGE,"c4719064-44fe-4252-b3a6-de5fb7a830d2"),sQuery(id+"F0.wireOp",EDGE,"0bf6103d-bcda-4bbf-96c7-54e6ef03cde9"),sQuery(id+"F0.wireOp",EDGE,"e9d37db2-ae33-474e-9755-d6a2f55bc904"),sQuery(id+"F0.wireOp",EDGE,"E0.top"),sQuery(id+"F0.wireOp",EDGE,"E0.left"),sQuery(id+"F0.wireOp",EDGE,"E0.right")])],"isStart":false}),makeQuery(id+"F3.opExtrude","SWEPT_FACE",FACE,{"disambiguationData":[OSD([sQuery(id+"F2.wireOp",EDGE,"E132.bottom")])]})]});
            var sketch = newSketch(context, id + "F4", { "sketchPlane" : qUnion([Q0])});
            skLineSegment(sketch, "E134.bottom", {"start": v(-3.74, 114.68) * mm, "end": v(1.26, 114.68) * mm, "construction": true});
            skLineSegment(sketch, "E134.top", {"start": v(-3.74, 104.68) * mm, "end": v(1.26, 104.68) * mm, "construction": true});
            skLineSegment(sketch, "E134.left", {"start": v(-3.74, 114.68) * mm, "end": v(-3.74, 104.68) * mm, "construction": true});
            skLineSegment(sketch, "E134.right", {"start": v(1.26, 114.68) * mm, "end": v(1.26, 104.68) * mm, "construction": true});
            skPoint(sketch, "E135", {"position": v(-1.24, 114.68) * mm});
            skLineSegment(sketch, "E136", {"start": v(-1.24, 114.68) * mm, "end": v(-1.24, 108.68) * mm, "construction": true});
            skLineSegment(sketch, "E137", {"start": v(-2.24, 114.68) * mm, "end": v(-0.24, 114.68) * mm});
            skLineSegment(sketch, "E138", {"start": v(-2.74, 108.68) * mm, "end": v(0.26, 108.68) * mm});
            skPoint(sketch, "E139", {"position": v(-1.24, 108.68) * mm});
            skLineSegment(sketch, "E140", {"start": v(-2.24, 114.68) * mm, "end": v(-2.74, 108.68) * mm});
            skLineSegment(sketch, "E141", {"start": v(-0.24, 114.68) * mm, "end": v(0.26, 108.68) * mm});
            skLineSegment(sketch, "E142.bottom", {"start": v(-5.74, 114.68) * mm, "end": v(3.26, 114.68) * mm});
            skLineSegment(sketch, "E142.top", {"start": v(-5.74, 104.68) * mm, "end": v(3.26, 104.68) * mm});
            skLineSegment(sketch, "E142.left", {"start": v(-5.74, 114.68) * mm, "end": v(-5.74, 104.68) * mm});
            skLineSegment(sketch, "E142.right", {"start": v(3.26, 114.68) * mm, "end": v(3.26, 104.68) * mm});
            skSolve(sketch);
        }
        {
            var Q0;
            {var subQ3=sQuery(id+"F4.wireOp",EDGE,"E142.left");Q0=makeQuery(id+"F4.imprint","IMPRINT",FACE,{"disambiguationData":[TD([[makeQuery(id+"F4.imprint","IMPRINT",EDGE,{"derivedFrom":subQ3}),1.0]])]});}
            var Q1;
            {var subQ3=sQuery(id+"F4.wireOp",EDGE,"E142.right");Q1=makeQuery(id+"F4.imprint","IMPRINT",FACE,{"disambiguationData":[TD([[makeQuery(id+"F4.imprint","IMPRINT",EDGE,{"derivedFrom":subQ3}),-1.0]])]});}
            extrude(context, id + "F5", {"entities" : qUnion([Q0, Q1]), "operationType" : NewBodyOperationType.ADD, "oppositeDirection" : true, "depth" : 5 * mm});
        }
        {
            var Q0;
            Q0=makeQuery(id+"F4.imprint","IMPRINT",FACE,{"disambiguationData":[TD([[makeQuery(id+"F4.imprint","IMPRINT",EDGE,{"derivedFrom":sQuery(id+"F4.wireOp",EDGE,"E138")}),1.0]])]});
            extrude(context, id + "F6", {"entities" : qUnion([Q0]), "operationType" : NewBodyOperationType.REMOVE, "oppositeDirection" : true, "depth" : 5 * mm});
        }
        {
            var Q0;
            Q0=makeQuery(id+"F5.opExtrude","SWEPT_FACE",FACE,{"disambiguationData":[OSD([sQuery(id+"F4.wireOp",EDGE,"E142.right")])]});
            var sketch = newSketch(context, id + "F7", { "sketchPlane" : qUnion([Q0])});
            skLineSegment(sketch, "E143.top", {"start": v(124.03, 0) * mm, "end": v(118.03, 0) * mm, "construction": true});
            skLineSegment(sketch, "E143.right", {"start": v(118.03, 5) * mm, "end": v(118.03, 0) * mm, "construction": true});
            skLineSegment(sketch, "E144", {"start": v(121.03, 0) * mm, "end": v(121.03, 5) * mm, "construction": true});
            skCircle(sketch, "E145", {"center": v(121.03, 2.5) * mm, "radius": 1 * mm});
            skSolve(sketch);
        }
        {
            var Q0;
            Q0=qSketchRegion(id+"F7",true);
            extrude(context, id + "F8", {"entities" : qUnion([Q0]), "operationType" : NewBodyOperationType.REMOVE, "oppositeDirection" : true, "depth" : 10 * mm});
        }
    });
